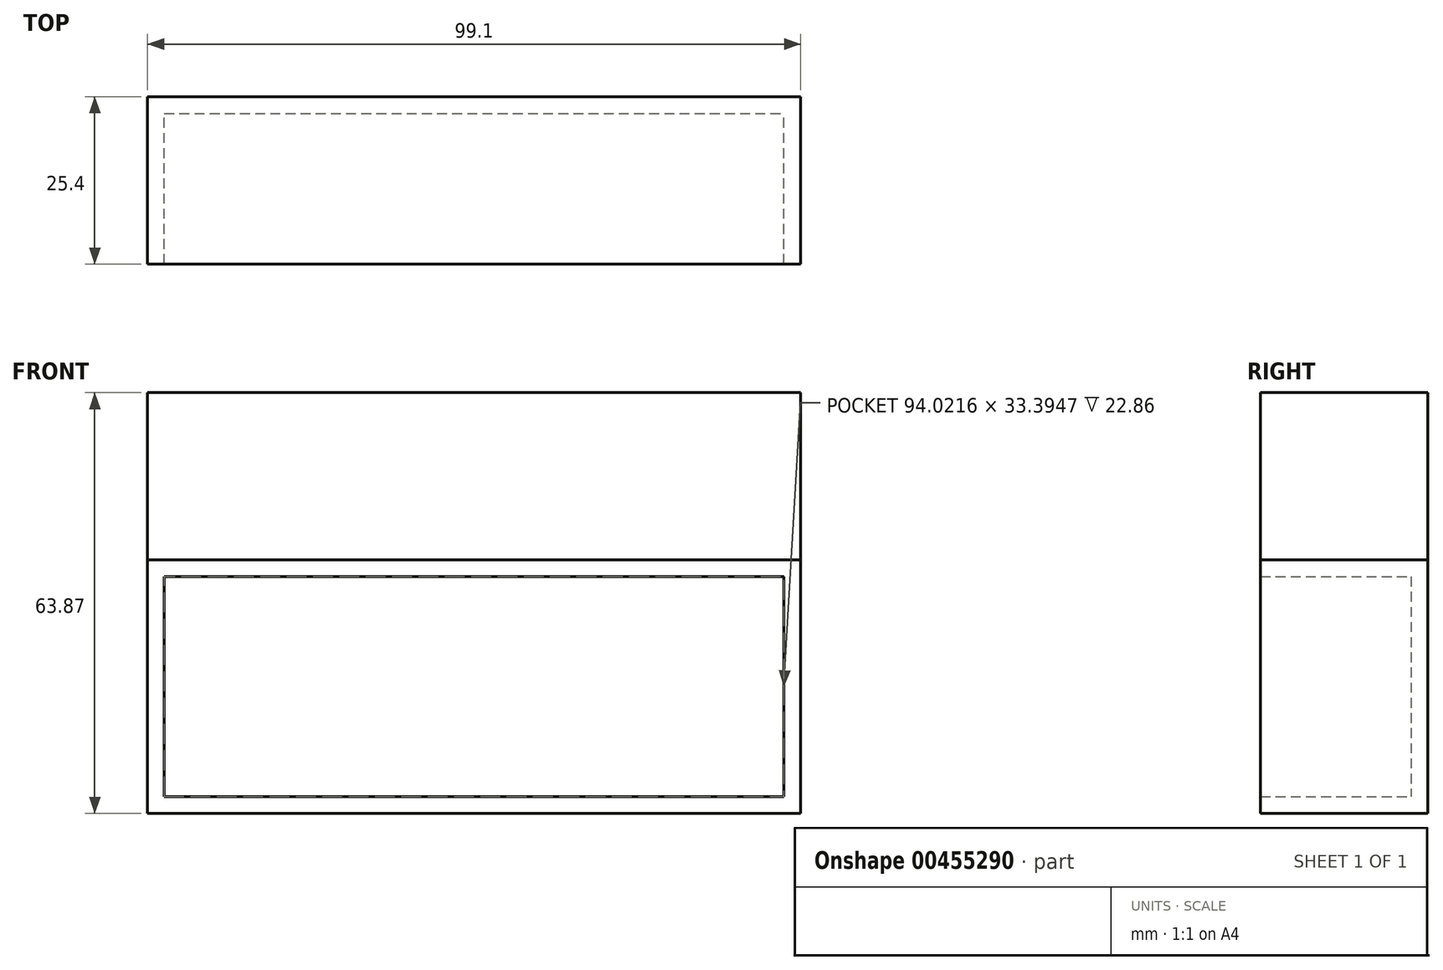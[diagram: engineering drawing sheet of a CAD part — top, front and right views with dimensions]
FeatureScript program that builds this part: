
annotation { "Feature Type Name" : "Feature", "Feature Type Description" : "" }
export const myFeature = defineFeature(function(context is Context, id is Id, definition is map)
    precondition{}
    {
        {
            var Q0;
            Q0=qCreatedBy(makeId("Front.planeOp"),FACE);
            var sketch = newSketch(context, id + "F0", { "sketchPlane" : qUnion([Q0])});
            skLineSegment(sketch, "E0.bottom", {"start": v(-46.34, 13.26) * mm, "end": v(52.76, 13.26) * mm});
            skLineSegment(sketch, "E0.top", {"start": v(-46.34, -25.21) * mm, "end": v(52.76, -25.21) * mm});
            skLineSegment(sketch, "E0.left", {"start": v(-46.34, 13.26) * mm, "end": v(-46.34, -25.21) * mm});
            skLineSegment(sketch, "E0.right", {"start": v(52.76, 13.26) * mm, "end": v(52.76, -25.21) * mm});
            skSolve(sketch);
        }
        {
            var Q0;
            Q0=makeQuery(id+"F0.imprint","IMPRINT",FACE,{"disambiguationData":[TD([[makeQuery(id+"F0.imprint","IMPRINT",EDGE,{"derivedFrom":sQuery(id+"F0.wireOp",EDGE,"E0.bottom")}),-1.0]])]});
            extrude(context, id + "F1", {"entities" : qUnion([Q0]), "depth" : 25.4 * mm});
        }
        {
            var Q0;
            Q0=makeQuery(id+"F1.opExtrude","SWEPT_FACE",FACE,{"disambiguationData":[OSD([sQuery(id+"F0.wireOp",EDGE,"E0.bottom")])]});
            extrude(context, id + "F2", {"entities" : qUnion([Q0]), "depth" : 25.4 * mm});
        }
        {
            var Q0;
            Q0=makeQuery(id+"F1.opExtrude","CAP_FACE",FACE,{"disambiguationData":[OSD([sQuery(id+"F0.wireOp",EDGE,"E0.bottom"),sQuery(id+"F0.wireOp",EDGE,"E0.top"),sQuery(id+"F0.wireOp",EDGE,"E0.left"),sQuery(id+"F0.wireOp",EDGE,"E0.right")])],"isStart":false});
            shell(context, id + "F3", {"entities" : qUnion([Q0]), "thickness" : 2.54 * mm});
        }
    });
